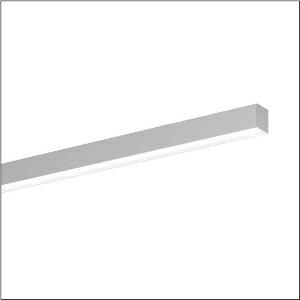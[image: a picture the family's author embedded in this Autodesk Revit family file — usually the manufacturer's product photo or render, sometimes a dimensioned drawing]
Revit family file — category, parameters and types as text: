
# Revit family: silica_r__21_51mx20db32sb_b045
name_source: partatom
category: Lighting Fixtures
units: mm (PartAtom-declared; Revit-internal decimal feet)

## family parameters
Cut with Voids When Loaded = No
Host = Face
Light Source = No
Part Type = Normal
Room Calculation Point = No
Round Connector Dimension = Use Diameter
Shared = No

## types (1)
- --- (1 x LED, 3000 lm, 20.2 W, 3000K)
    Apparent Load = 20 VA
    CIE Flux Codes = 48 79 96 100 100
    Color Rendering = 80
    Color Temperature = 3000K
    Default Elevation = 1800 mm
    Description = Silica® 21, office luminaire, primary optical cover: cover, of PMMA, opal, light emission: direct distribution, primary light characteristic: symmetric, installation type: surface-mounted, LED, rated luminous flux: 3.000lm, luminous efficacy: 149lm/W, light colour: 830, colour temperature: 3000K, with terminal, 3+2-pole, max. 2.5mm², mains connection: 220..240V, AC, 50/60Hz, luminaire housing, of aluminium, metallic grey (RAL 9006), length: 1.504mm, width: 53mm, height: 53mm, protection rating (complete): IP20, insulation class (complete): insulation class I (protective earthing), certification: CE, permissible operating ambient temperature: 0..+35°C, standard: EN 50419, packaging unit: 1 piece
    Height = 0 mm  [stored 0 ft]
    Lamp = 1 x LED
    Lamp Light Flux = 3000 lm
    Lamp Power = 20.2 W
    Lamp count = 1
    Length = 1504 mm
    Luminous efficacy = 149 lm/W
    Manufacturer = Siteco
    ModVariant = No
    Model = 51MX20DB32SB
    Mounting Place = Ceiling
    Mounting Type = Recessed
    Number of Poles = 1
    OnlyDefault = Yes
    Power Factor = 1
    Product Name = Silica® 21
    Product group = office luminaire | ceiling recessed
    ProductGroupID = 401
    Protection Class = Protection class I
    Protection Degree = IP 20
    RLX_Detail_Level = 1
    RLX_Emergency_Light_Flux = 0 lm
    RLX_Emergency_Type = 0
    RLX_Emergency_Type_DB = No
    RlxData = <blob elided: 26109 chars, md5=563ed3ef>
    Socket = socket
    Standby Power = 0 W
    System Light Flux = 3000 lm
    System Power = 20 W
    Type Comments = factory setting: luminous flux: 100 % | dim-lin: 254 | 233 mA
    Type Image = l_1297768.jpg
    URL = http://relux.com
    VarID = @adj_048089
    Voltage = 0 V
    Weight = 0.00 kg
    Width = 53 mm

note: [stored X ft] marks values corroborated as IEEE doubles in the binary element streams (Revit-internal decimal feet)

## geometry (parser evidence)
native form markers: Blend x4, Sweep x11
no freeform markers — native parametric forms only
